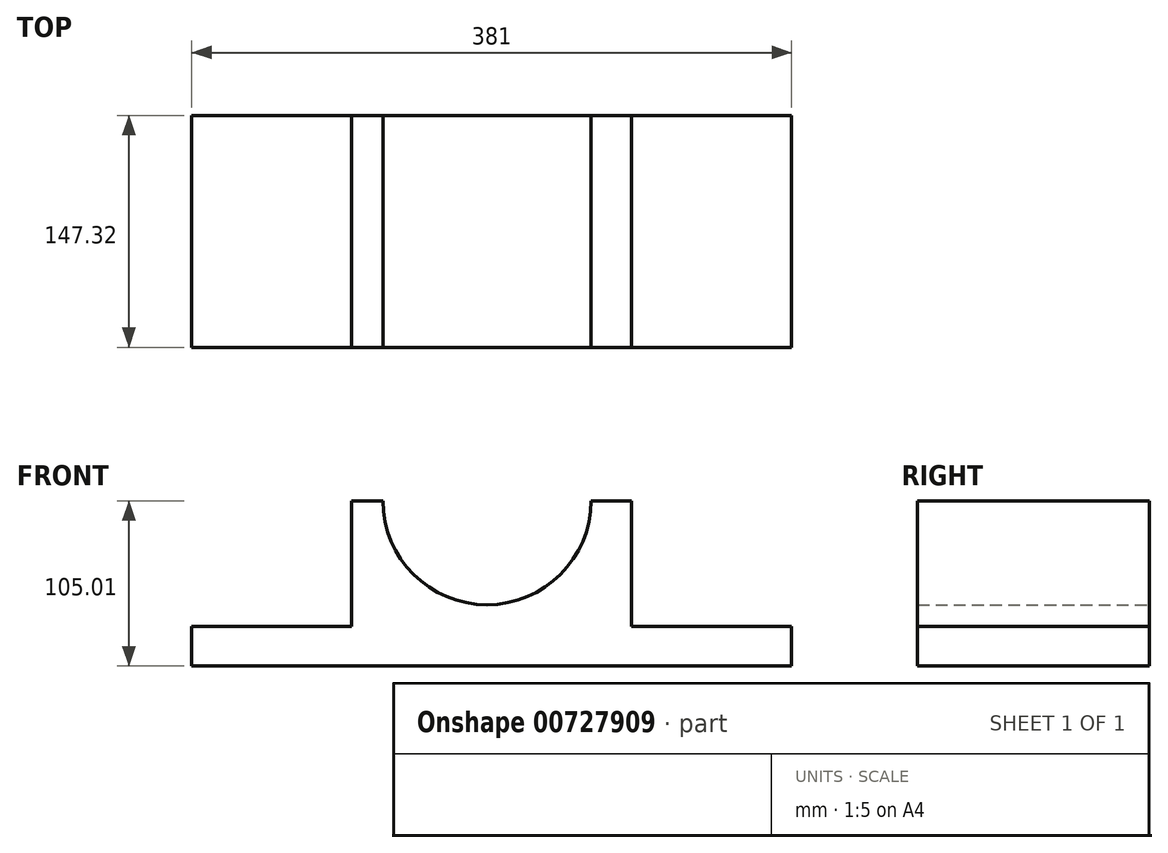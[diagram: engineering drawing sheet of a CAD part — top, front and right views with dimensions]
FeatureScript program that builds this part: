
annotation { "Feature Type Name" : "Feature", "Feature Type Description" : "" }
export const myFeature = defineFeature(function(context is Context, id is Id, definition is map)
    precondition{}
    {
        {
            var Q0;
            Q0=qCreatedBy(makeId("Front.planeOp"),FACE);
            var sketch = newSketch(context, id + "F0", { "sketchPlane" : qUnion([Q0])});
            skLineSegment(sketch, "E0", {"start": v(-162.07, -23.45) * mm, "end": v(-60.47, -23.45) * mm});
            skLineSegment(sketch, "E1", {"start": v(-60.47, 56.46) * mm, "end": v(-60.47, -23.45) * mm});
            skLineSegment(sketch, "E2", {"start": v(-40.66, 56.46) * mm, "end": v(-60.47, 56.46) * mm});
            skLineSegment(sketch, "E3", {"start": v(-162.07, -23.45) * mm, "end": v(-162.07, -48.55) * mm});
            skLineSegment(sketch, "E4", {"start": v(-162.07, -48.55) * mm, "end": v(218.93, -48.55) * mm});
            skLineSegment(sketch, "E5", {"start": v(218.93, -48.55) * mm, "end": v(218.93, -23.45) * mm});
            skLineSegment(sketch, "E6", {"start": v(218.93, -23.45) * mm, "end": v(117.33, -23.45) * mm});
            skLineSegment(sketch, "E7", {"start": v(117.33, -23.45) * mm, "end": v(117.33, 56.46) * mm});
            skArc(sketch, "E8", {"start": v(-40.66, 56.46) * mm, "mid": v(25.38, -9.58) * mm, "end": v(91.42, 56.46) * mm});
            skLineSegment(sketch, "E9", {"start": v(91.42, 56.46) * mm, "end": v(117.33, 56.46) * mm});
            skSolve(sketch);
        }
        {
            var Q0;
            Q0=makeQuery(id+"F0.imprint","IMPRINT",FACE,{"disambiguationData":[TD([[makeQuery(id+"F0.imprint","IMPRINT",EDGE,{"derivedFrom":sQuery(id+"F0.wireOp",EDGE,"E0")}),-1.0]])]});
            extrude(context, id + "F1", {"entities" : qUnion([Q0]), "depth" : 147.32 * mm, "offsetDistance" : 25.4 * mm});
        }
    });
